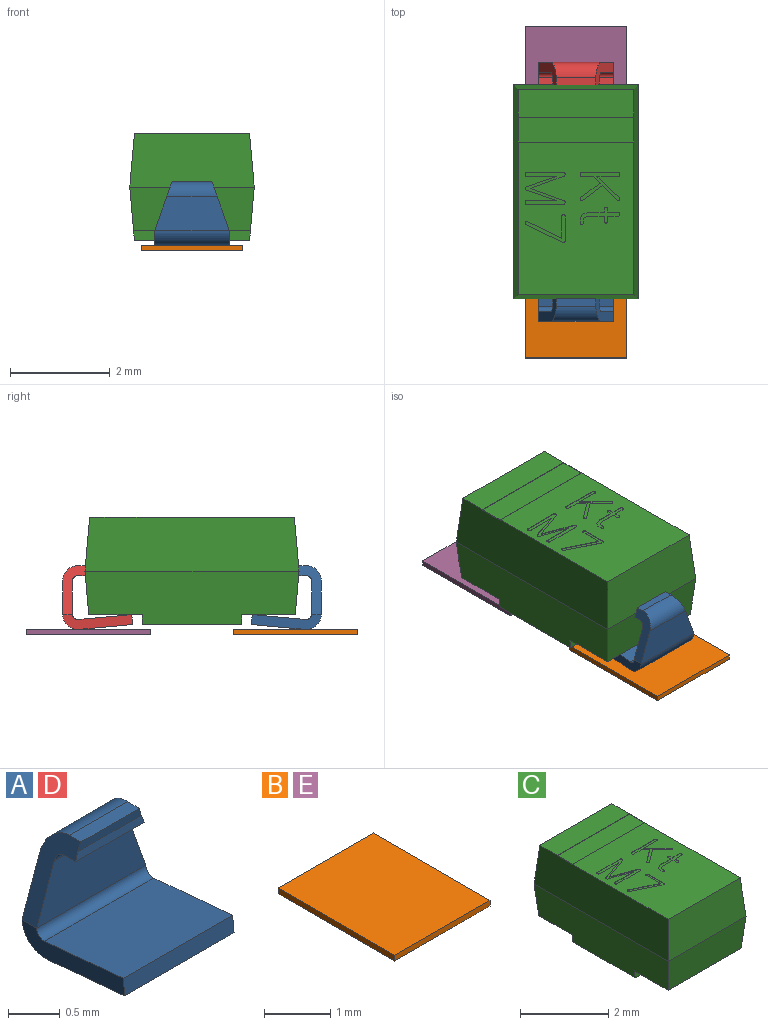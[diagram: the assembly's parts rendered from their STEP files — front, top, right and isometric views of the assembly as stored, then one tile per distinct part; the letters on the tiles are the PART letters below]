
ASSEMBLY  parts=5 mates=4
PART A: 18 faces, bbox 1.5x1.4x1.3 mm
  f0: plane 1.5x0.68mm, normal (0,1,0), area 0.9mm2, adj f1,f13,f16,f17
  f1: cylinder r=0.3mm len=1.01mm, axis (1,0,0), area 0.4mm2, adj f0,f2,f16,f17
  f2: plane 0.8x0.16mm, normal (0,0,1), area 0.1mm2, adj f1,f3,f16,f17
  f3: plane 0.88x0.11mm, normal (0,-1,-0.09), area 0.1mm2, adj f2,f4,f16,f17
  f4: plane 0.94x0.1mm, normal (0,-1,0.09), area 0.1mm2, adj f3,f5,f16,f17
  f5: plane 0.94x0.16mm, normal (0,0,-1), area 0.1mm2, adj f4,f6,f16,f17
  f6: cylinder r=0.1mm len=1.01mm, axis (1,0,0), area 0.2mm2, adj f5,f7,f16,f17
  f7: plane 1.5x0.68mm, normal (0,-1,0), area 0.9mm2, adj f6,f15,f16,f17
  f8: plane 1.41x0.3mm, normal (-1,0,0), area 0.3mm2, adj f9,f10,f11,f12,f13,f15,f17
  f9: plane 1.5x1.08mm, normal (0,0.09,1), area 1.6mm2, adj f8,f10,f14,f15
  f10: plane 1.5x0.2mm, normal (0,-1,0.09), area 0.3mm2, adj f8,f9,f11,f14
  f11: plane 1.5x1.04mm, normal (0,-0.09,-1), area 1.6mm2, adj f8,f10,f12,f14
  f12: plane 1.5x0.1mm, normal (0,0,-1), area 0.2mm2, adj f8,f11,f13,f14
  f13: cylinder r=0.32mm len=1.5mm, axis (1,0,0), area 0.6mm2, adj f0,f8,f12,f14
  f14: plane 1.41x0.3mm, normal (1,0,0), area 0.3mm2, adj f9,f10,f11,f12,f13,f15,f16
  f15: cylinder r=0.1mm len=1.5mm, axis (1,0,0), area 0.2mm2, adj f7,f8,f9,f14
  f16: plane 1x0.47mm, normal (0.94,0,0.34), area 0.2mm2, adj f0,f1,f2,f3,f4,f5,f6,f7
  f17: plane 1x0.47mm, normal (-0.94,0,0.34), area 0.2mm2, adj f0,f1,f2,f3,f4,f5,f6,f7
PART B: 6 faces, bbox 2x2.5x0.1 mm
  f0: plane 2.5x0.11mm, normal (-1,0,0), area 0.3mm2, adj f1,f3,f4,f5
  f1: plane 2.04x0.11mm, normal (0,-1,0), area 0.2mm2, adj f0,f2,f4,f5
  f2: plane 2.5x0.11mm, normal (1,0,0), area 0.3mm2, adj f1,f3,f4,f5
  f3: plane 2.04x0.11mm, normal (0,1,0), area 0.2mm2, adj f0,f2,f4,f5
  f4: plane 2.5x2.04mm, normal (0,0,-1), area 5.1mm2, adj f0,f1,f2,f3
  f5: plane 2.5x2.04mm, normal (0,0,1), area 5.1mm2, adj f0,f1,f2,f3
PART C: 107 faces, bbox 2.5x4.3x2.2 mm
  f0: plane 0.8x0.57mm, normal (0,0,1), area 0.1mm2, adj f8,f9,f10,f11,f12,f13,f14,f15
  f1: plane 0.8x0.36mm, normal (0,0,1), area 0.1mm2, adj f22,f23,f24,f25,f26,f27,f28,f29
  f2: plane 0.8x0.57mm, normal (0,0,1), area 0.1mm2, adj f50,f51,f52,f53,f54,f55,f56,f57
  f3: plane 0.8x0.64mm, normal (0,0,1), area 0.2mm2, adj f71,f72,f73,f74,f75,f76,f77,f78
  f4: plane 2.31x0.5mm, normal (0,0,1), area 1.2mm2, adj f5,f6,f7,f91
  f5: plane 2.31x0.01mm, normal (0,-1,0), area 0mm2, adj f4,f6,f7,f96
  f6: plane 0.5x0.01mm, normal (-1,0,0), area 0mm2, adj f4,f5,f91,f97
  f7: plane 0.5x0.01mm, normal (1,0,0), area 0mm2, adj f4,f5,f91,f98
  f8: plane 0.49x0.01mm, normal (-1,0,0), area 0mm2, adj f0,f9,f21,f99
  f9: plane 0.01x0.01mm, normal (-1,-0.1,0), area 0mm2, adj f0,f8,f10,f99
  f10: cylinder r=0.04mm len=0.04mm, axis (0,0,-1), area 0mm2, adj f0,f9,f11,f99
  f11: cylinder r=0.02mm len=0.03mm, axis (0,0,-1), area 0mm2, adj f0,f10,f12,f99
  f12: plane 0.46x0.01mm, normal (1,0,0), area 0mm2, adj f0,f11,f13,f99
  f13: plane 0.69x0.33mm, normal (-0.44,-0.9,0), area 0mm2, adj f0,f12,f14,f99
  f14: cylinder r=0.03mm len=0.02mm, axis (0,0,-1), area 0mm2, adj f0,f13,f15,f99
  f15: cylinder r=0.01mm len=0.01mm, axis (0,0,-1), area 0mm2, adj f0,f14,f16,f99
  f16: extruded ~0.03x0.02mm, area 0mm2, adj f0,f15,f17,f99
  f17: extruded ~0.04x0.02mm, area 0mm2, adj f0,f16,f18,f99
  f18: plane 0.73x0.35mm, normal (0.44,0.9,0), area 0mm2, adj f0,f17,f19,f99
  f19: plane 0.02x0.01mm, normal (0.36,0.93,0), area 0mm2, adj f0,f18,f20,f99
  f20: cylinder r=0.04mm len=0.03mm, axis (0,0,-1), area 0mm2, adj f0,f19,f21,f99
  f21: cylinder r=0.05mm len=0.03mm, axis (0,0,-1), area 0mm2, adj f0,f8,f20,f99
  f22: extruded ~0.03x0.02mm, area 0mm2, adj f1,f23,f49,f99
  f23: plane 0.22x0.01mm, normal (0,-1,0), area 0mm2, adj f1,f22,f24,f99
  f24: plane 0.06x0.01mm, normal (-1,0,0), area 0mm2, adj f1,f23,f25,f99
  f25: extruded ~0.04x0.02mm, area 0mm2, adj f1,f24,f26,f99
  f26: cylinder r=0.04mm len=0.01mm, axis (0,0,-1), area 0mm2, adj f1,f25,f27,f99
  f27: extruded ~0.03x0.03mm, area 0mm2, adj f1,f26,f28,f99
  f28: plane 0.08x0.01mm, normal (1,0,0), area 0mm2, adj f1,f27,f29,f99
  f29: plane 0.32x0.01mm, normal (0,-1,0), area 0mm2, adj f1,f28,f30,f99
  f30: plane 0.12x0.04mm, normal (0.31,-0.95,0), area 0mm2, adj f1,f29,f31,f99
  f31: plane 0.01x0.01mm, normal (0.65,-0.76,0), area 0mm2, adj f1,f30,f32,f99
  f32: plane 0.08x0.04mm, normal (0.9,-0.44,0), area 0mm2, adj f1,f31,f33,f99
  f33: plane 0.09x0.01mm, normal (1,0,0), area 0mm2, adj f1,f32,f34,f99
  f34: extruded ~0.03x0.02mm, area 0mm2, adj f1,f33,f35,f99
  f35: cylinder r=0.03mm len=0.02mm, axis (0,0,-1), area 0mm2, adj f1,f34,f36,f99
  f36: extruded ~0.03x0.03mm, area 0mm2, adj f1,f35,f37,f99
  f37: plane 0.07x0.01mm, normal (-1,0,0), area 0mm2, adj f1,f36,f38,f99
  f38: plane 0.05x0.02mm, normal (-0.9,0.44,0), area 0mm2, adj f1,f37,f39,f99
  f39: plane 0.08x0.03mm, normal (-0.33,0.95,0), area 0mm2, adj f1,f38,f40,f99
  f40: plane 0.31x0.01mm, normal (0,1,0), area 0mm2, adj f1,f39,f41,f99
  f41: plane 0.11x0.01mm, normal (1,0,0), area 0mm2, adj f1,f40,f42,f99
  f42: extruded ~0.03x0.02mm, area 0mm2, adj f1,f41,f43,f99
  f43: cylinder r=0.06mm len=0.02mm, axis (0,0,-1), area 0mm2, adj f1,f42,f44,f99
  f44: cylinder r=0.05mm len=0.02mm, axis (0,0,-1), area 0mm2, adj f1,f43,f45,f99
  f45: cylinder r=0.04mm len=0.03mm, axis (0,0,-1), area 0mm2, adj f1,f44,f46,f99
  f46: plane 0.11x0.01mm, normal (-1,0,0), area 0mm2, adj f1,f45,f47,f99
  f47: plane 0.21x0.01mm, normal (0,1,0), area 0mm2, adj f1,f46,f48,f99
  f48: cylinder r=0.03mm len=0.02mm, axis (0,0,-1), area 0mm2, adj f1,f47,f49,f99
  f49: bspline ~0.04x0.01mm, area 0mm2, adj f1,f22,f48,f99
  f50: cylinder r=0.07mm len=0.02mm, axis (0,0,-1), area 0mm2, adj f2,f51,f70,f99
  f51: cylinder r=0.03mm len=0.02mm, axis (0,0,-1), area 0mm2, adj f2,f50,f52,f99
  f52: plane 0.46x0.43mm, normal (-0.69,-0.72,0), area 0mm2, adj f2,f51,f53,f99
  f53: plane 0.43x0.01mm, normal (0,1,0), area 0mm2, adj f2,f52,f54,f99
  f54: extruded ~0.04x0.03mm, area 0mm2, adj f2,f53,f55,f99
  f55: plane 0.02x0.01mm, normal (-0.98,-0.17,0), area 0mm2, adj f2,f54,f56,f99
  f56: extruded ~0.02x0.02mm, area 0mm2, adj f2,f55,f57,f99
  f57: plane 0.73x0.01mm, normal (0,-1,0), area 0mm2, adj f2,f56,f58,f99
  f58: cylinder r=0.03mm len=0.04mm, axis (0,0,-1), area 0mm2, adj f2,f57,f59,f99
  f59: extruded ~0.04x0.02mm, area 0mm2, adj f2,f58,f60,f99
  f60: plane 0.24x0.01mm, normal (0,1,0), area 0mm2, adj f2,f59,f61,f99
  f61: plane 0.14x0.13mm, normal (0.68,0.73,0), area 0mm2, adj f2,f60,f62,f99
  f62: plane 0.4x0.29mm, normal (0.59,-0.81,0), area 0mm2, adj f2,f61,f63,f99
  f63: cylinder r=0.03mm len=0.02mm, axis (0,0,-1), area 0mm2, adj f2,f62,f64,f99
  f64: cylinder r=0.05mm len=0.04mm, axis (0,0,-1), area 0mm2, adj f2,f63,f65,f99
  f65: cylinder r=0.06mm len=0.01mm, axis (0,0,-1), area 0mm2, adj f2,f64,f66,f99
  f66: plane 0.01x0.01mm, normal (-0.31,0.95,0), area 0mm2, adj f2,f65,f67,f99
  f67: plane 0.41x0.31mm, normal (-0.6,0.8,0), area 0mm2, adj f2,f66,f68,f99
  f68: plane 0.31x0.31mm, normal (0.71,0.71,0), area 0mm2, adj f2,f67,f69,f99
  f69: cylinder r=0.02mm len=0.02mm, axis (0,0,-1), area 0mm2, adj f2,f68,f70,f99
  f70: extruded ~0.03x0.03mm, area 0mm2, adj f2,f50,f69,f99
  f71: cylinder r=0.03mm len=0.03mm, axis (0,0,-1), area 0mm2, adj f3,f72,f90,f99
  f72: plane 0.73x0.01mm, normal (0,-1,0), area 0mm2, adj f3,f71,f73,f99
  f73: cylinder r=0.03mm len=0.04mm, axis (0,0,-1), area 0mm2, adj f3,f72,f74,f99
  f74: extruded ~0.04x0.02mm, area 0mm2, adj f3,f73,f75,f99
  f75: plane 0.61x0.01mm, normal (0,1,0), area 0mm2, adj f3,f74,f76,f99
  f76: plane 0.62x0.21mm, normal (0.32,-0.95,0), area 0mm2, adj f3,f75,f77,f99
  f77: plane 0.01x0.01mm, normal (0.65,-0.76,0), area 0mm2, adj f3,f76,f78,f99
  f78: extruded ~0.03x0.01mm, area 0mm2, adj f3,f77,f79,f99
  f79: extruded ~0.03x0.02mm, area 0mm2, adj f3,f78,f80,f99
  f80: plane 0.62x0.21mm, normal (0.32,0.95,0), area 0mm2, adj f3,f79,f81,f99
  f81: plane 0.6x0.01mm, normal (0,-1,0), area 0mm2, adj f3,f80,f82,f99
  f82: cylinder r=0.03mm len=0.03mm, axis (0,0,-1), area 0mm2, adj f3,f81,f83,f99
  f83: extruded ~0.04x0.03mm, area 0mm2, adj f3,f82,f84,f99
  f84: plane 0.75x0.01mm, normal (0,1,0), area 0mm2, adj f3,f83,f85,f99
  f85: plane 0.01x0.01mm, normal (-0.24,0.97,0), area 0mm2, adj f3,f84,f86,f99
  f86: extruded ~0.04x0.02mm, area 0mm2, adj f3,f85,f87,f99
  f87: cylinder r=0.03mm len=0.03mm, axis (0,0,-1), area 0mm2, adj f3,f86,f88,f99
  f88: plane 0.69x0.25mm, normal (-0.35,-0.94,0), area 0mm2, adj f3,f87,f89,f99
  f89: plane 0.68x0.25mm, normal (-0.34,0.94,0), area 0mm2, adj f3,f88,f90,f99
  f90: cylinder r=0.04mm len=0.04mm, axis (0,0,-1), area 0mm2, adj f3,f71,f89,f99
  f91: plane 2.31x0.01mm, normal (0,1,0), area 0mm2, adj f4,f6,f7,f99
  f92: plane 2.35x0.2mm, normal (0,-1,0), area 0.5mm2, adj f93,f100,f101,f104
  f93: plane 2.31x2mm, normal (0,0,-1), area 4.6mm2, adj f92,f94,f100,f104
  f94: plane 2.35x0.2mm, normal (0,1,0), area 0.5mm2, adj f93,f95,f100,f104
  f95: plane 2.35x1.07mm, normal (0,0,-1), area 2.5mm2, adj f94,f100,f103,f104
  f96: plane 2.31x0.56mm, normal (0,0,1), area 1.3mm2, adj f5,f97,f98,f102
  f97: plane 4.3x1.08mm, normal (1,0,0.09), area 4.5mm2, adj f6,f96,f99,f100,f102,f106
  f98: plane 4.3x1.08mm, normal (-1,0,0.09), area 4.5mm2, adj f7,f96,f99,f102,f104,f106
  f99: plane 3.06x2.31mm, normal (0,0,1), area 6.6mm2, adj f8,f9,f10,f11,f12,f13,f14,f15
  f100: plane 4.3x1.08mm, normal (1,0,-0.09), area 4.1mm2, adj f92,f93,f94,f95,f97,f101,f103,f105
  f101: plane 2.35x1.07mm, normal (0,0,-1), area 2.5mm2, adj f92,f100,f104,f105
  f102: plane 2.5x1.08mm, normal (0,1,0.09), area 2.6mm2, adj f96,f97,f98,f103
  f103: plane 2.5x0.88mm, normal (0,1,-0.09), area 2.1mm2, adj f95,f100,f102,f104
  f104: plane 4.3x1.08mm, normal (-1,0,-0.09), area 4.1mm2, adj f92,f93,f94,f95,f98,f101,f103,f105
  f105: plane 2.5x0.88mm, normal (0,-1,-0.09), area 2.1mm2, adj f100,f101,f104,f106
  f106: plane 2.5x1.08mm, normal (0,-1,0.09), area 2.6mm2, adj f97,f98,f99,f105
PART D: same geometry as A
PART E: same geometry as B
PLACE A rot(axis=(0,0,-1),180deg) t=(-5.59,43.18,0)mm
PLACE B rot(axis=(0,0,1),180deg) t=(-5.59,43.17,0)mm
PLACE C at identity
PLACE D at identity
PLACE E at identity
MATE fastened A.f4 <-> C.f105  axis (0,1,0.09) through (-2.79,19.44,1.28)mm
MATE fastened D.f12 <-> E.f5  axis (0,0,-1) through (-2.79,23.92,0.11)mm
MATE fastened C.f103 <-> D.f4  axis (0,1,-0.09) through (-2.79,23.74,1.28)mm
MATE fastened A.f12 <-> B.f5  axis (0,0,-1) through (-2.79,19.25,0.11)mm
